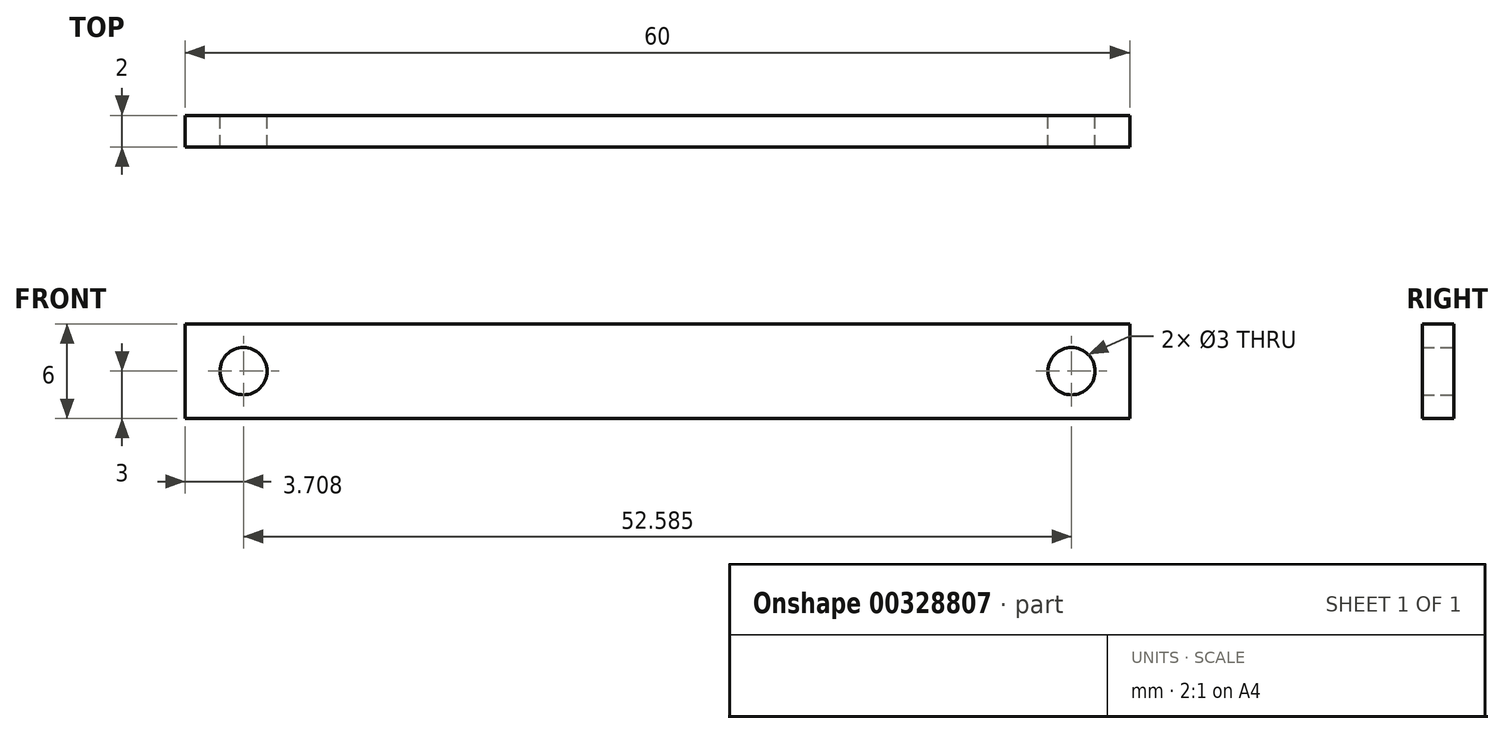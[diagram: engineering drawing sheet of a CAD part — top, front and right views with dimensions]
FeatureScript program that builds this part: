
annotation { "Feature Type Name" : "Feature", "Feature Type Description" : "" }
export const myFeature = defineFeature(function(context is Context, id is Id, definition is map)
    precondition{}
    {
        {
            var Q0;
            Q0=qCreatedBy(makeId("Front.planeOp"),FACE);
            var sketch = newSketch(context, id + "F0", { "sketchPlane" : qUnion([Q0])});
            skLineSegment(sketch, "E0.bottom", {"start": v(30, 3) * mm, "end": v(-30, 3) * mm});
            skLineSegment(sketch, "E0.top", {"start": v(30, -3) * mm, "end": v(-30, -3) * mm});
            skLineSegment(sketch, "E0.left", {"start": v(30, 3) * mm, "end": v(30, -3) * mm});
            skLineSegment(sketch, "E0.right", {"start": v(-30, 3) * mm, "end": v(-30, -3) * mm});
            skPoint(sketch, "E0.middle", {"position": v(0, 0) * mm});
            skCircle(sketch, "E1", {"center": v(-26.3, 0) * mm, "radius": 1.5 * mm});
            skCircle(sketch, "E2", {"center": v(26.3, 0) * mm, "radius": 1.5 * mm});
            skSolve(sketch);
        }
        {
            var Q0;
            Q0 = qSketchRegion(id + "F0", true);
            extrude(context, id + "F1", {"entities" : qUnion([Q0]), "depth" : 1 * mm, "hasSecondDirection" : true, "secondDirectionOppositeDirection" : true, "secondDirectionDepth" : 1 * mm});
        }
    });
